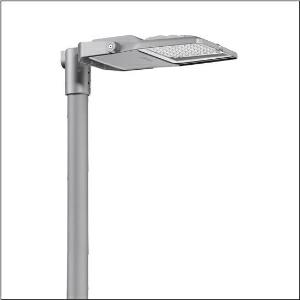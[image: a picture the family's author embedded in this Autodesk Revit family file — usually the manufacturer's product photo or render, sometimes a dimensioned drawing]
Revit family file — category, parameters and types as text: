
# Revit family: floodlight_fl_21_mini___pl61_5xa7775d2c3a_f3a4
name_source: partatom
category: Lighting Fixtures
units: mm (PartAtom-declared; Revit-internal decimal feet)

## family parameters
Cut with Voids When Loaded = No
Host = Face
Light Source = No
Part Type = Normal
Room Calculation Point = No
Round Connector Dimension = Use Diameter
Shared = No

## types (1)
- --- (1 x LED, 17510 lm, 142.9 W, 3000K)
    Apparent Load = 143 VA
    CIE Flux Codes = 33 65 98 100 100
    Color Rendering = 70
    Color Temperature = 3000K
    Default Elevation = 1800 mm
    Description = Floodlight FL 21 mini, floodlight, primary light control with lens, of PMMA, primary optical cover: protective disc, of toughened safety glass, transparent, light distribution: PL61, light emission: direct distribution, installation type: surface-mounted, LED, High Power LED, rated luminous flux: 17.510lm, luminous efficacy: 123lm/W, light colour: 730, colour temperature: 3000K, control: flexible luminous flux parameterisation, time-dependent luminous flux control, constant luminous flux control, overheat protection, pre-setting: logarithmic dimming characteristic, with terminal, 6-pole, mains connection: 220..240V, AC, 50/60Hz, start of lifetime: 143W, end of service life: 151W, reduction: 63W, luminaire housing, of diecast aluminium, powder-coated, Siteco® metallic grey (DB 702S), corrosivity category C5 mid according to DIN EN ISO 12944, sealing non-destructively replaceable, please order mast flange separately, mast bracket, of steel, galvanised, powder-coated, Siteco® metallic grey (DB 702S), Smart Interface above, protection rating (complete): IP66, insulation class (complete): insulation class II (safety insulation), certification: CE, ENEC, VDE, protection symbol: D, impact resistance: IK08, permissible operating ambient temperature: -40..+40°C, permissible operating ambient temperature for outdoor applications: -40..+50°C, standard: DIN EN 12944, LABS conformity tested according to VDMA 24364:2018-05, packaging unit: 1 piece

Light Distribution: PL61
    Height = 70 mm
    Lamp = 1 x LED
    Lamp Light Flux = 17510 lm
    Lamp Power = 142.9 W
    Lamp count = 1
    Length = 485 mm
    Luminous efficacy = 123 lm/W
    Manufacturer = Siteco
    ModVariant = No
    Model = 5XA7775D2C3A
    Number of Poles = 1
    OnlyDefault = Yes
    Power Factor = 1
    Product Name = Floodlight FL 21 mini | PL61
    Product group = floodlight | pylon annexe
    ProductGroupID = 6200
    Protection Class = Protection class II
    Protection Degree = IP 66
    RLX_Detail_Level = 1
    RLX_Emergency_Light_Flux = 0 lm
    RLX_Emergency_Type = 0
    RLX_Emergency_Type_DB = No
    RlxData = <blob elided: 101473 chars, md5=4cb90a43>
    Socket = socket
    Standby Power = 0 W
    System Light Flux = 17510 lm
    System Power = 143 W
    Type Comments = factory setting: luminous flux: 100 % | dim-lin: 254 | 730 mA
    Type Image = l_1007125.jpg
    URL = http://relux.com
    VarID = @adj_143035
    Voltage = 0 V
    Weight = 0.00 kg
    Width = 337 mm

## geometry (parser evidence)
native form markers: Blend x4, Sweep x12
no freeform markers — native parametric forms only
